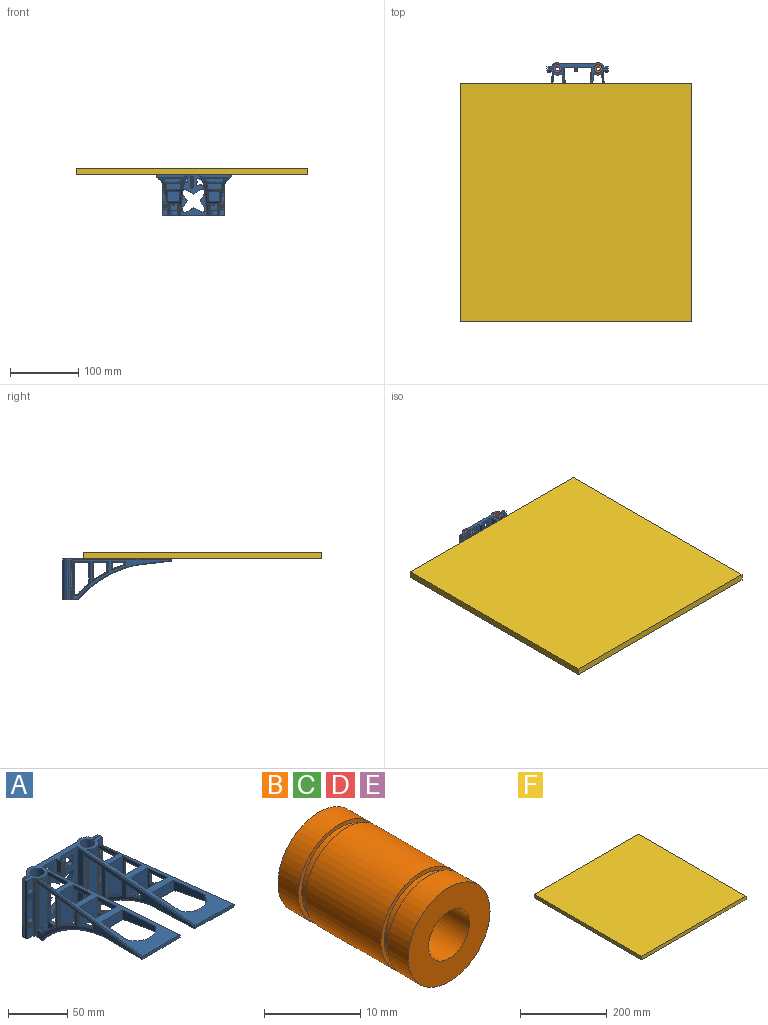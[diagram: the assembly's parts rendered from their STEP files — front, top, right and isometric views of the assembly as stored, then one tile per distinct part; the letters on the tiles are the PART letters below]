
ASSEMBLY  parts=6 mates=5
PART A: 310 faces, bbox 111.2x160.5x66.1 mm
  f0: plane 60x41.92mm, normal (0,-1,0), area 1382.5mm2, adj f11,f12,f14,f107,f146,f238,f266,f267
  f1: plane 21.16x6.51mm, normal (0,-1,0), area 128.2mm2, adj f36,f37,f131,f133
  f2: plane 10.58x6.51mm, normal (0,-1,0), area 64.1mm2, adj f11,f36,f37,f133
  f3: plane 10.58x6.51mm, normal (0,-1,0), area 64.1mm2, adj f12,f36,f37,f131
  f4: plane 23.21x4.1mm, normal (-1,-0.06,0), area 95.3mm2, adj f11,f17,f19,f86
  f5: plane 21.83x4.1mm, normal (1,-0.1,0), area 89.9mm2, adj f11,f17,f19,f89
  f6: extruded ~22.69x22.55mm, area 49.5mm2, adj f39,f43,f79,f81,f120,f121
  f7: plane 23.11x3.77mm, normal (0,0,-1), area 49.9mm2, adj f50,f52,f73,f85,f86
  f8: plane 21.34x15.62mm, normal (0,0,-1), area 35.5mm2, adj f39,f43,f70,f71,f119,f121
  f9: plane 60x2.08mm, normal (-1,0,0), area 124.6mm2, adj f11,f12,f35,f65
  f10: cylinder r=6.1mm len=60mm, axis (0,0,-1), area 2239.4mm2, adj f11,f12,f64,f65
  f11: plane 159.35x108.38mm, normal (0,0,1), area 4505.2mm2, adj f0,f2,f4,f5,f9,f10,f15,f16
  f12: plane 90.27x23.14mm, normal (0,0,-1), area 677.4mm2, adj f0,f3,f9,f10,f13,f14,f17,f18
  f13: plane 145.55x60.3mm, normal (-0.99,0.12,0), area 1183.5mm2, adj f12,f21,f37,f108,f109,f110,f111,f112
  f14: plane 153.23x60.08mm, normal (1,0.07,0), area 1761.4mm2, adj f0,f12,f21,f39,f40,f42,f44,f51
  f15: cylinder r=17.26mm len=31.2mm, axis (0,0,-1), area 201.1mm2, adj f11,f29,f38,f66
  f16: plane 21.95x20.78mm, normal (-1,-0.06,0), area 183mm2, adj f11,f30,f31,f61,f63,f68,f78,f100
  f17: cylinder r=9.14mm len=60mm, axis (0,0,-1), area 216.4mm2, adj f4,f5,f11,f12,f18,f23,f47,f51
  f18: plane 24.32x23.37mm, normal (-1,-0.06,0), area 130.6mm2, adj f12,f17,f20,f51,f83,f98,f99
  f19: plane 15.67x4.1mm, normal (0,1,0), area 64.2mm2, adj f4,f5,f11,f88
  f20: plane 16.84x5.3mm, normal (0,1,0), area 67.6mm2, adj f18,f23,f82,f83,f84,f99
  f21: plane 46.39x3.27mm, normal (0.01,-1,0), area 142.6mm2, adj f11,f13,f14,f44,f107,f108,f123
  f22: plane 22.01x21.64mm, normal (1,-0.1,0), area 196.6mm2, adj f11,f30,f31,f53,f55,f67,f77,f101
  f23: plane 23.03x22.24mm, normal (1,-0.1,0), area 124.3mm2, adj f12,f17,f20,f47,f82,f97,f99
  f24: plane 37.69x21.65mm, normal (-1,-0.06,0), area 181.2mm2, adj f11,f25,f26,f32,f42,f69,f80,f95
  f25: plane 19.91x4.1mm, normal (0,1,0), area 81.6mm2, adj f11,f24,f27,f71
  f26: plane 20.78x4.56mm, normal (0,1,0), area 74.7mm2, adj f24,f27,f79,f80,f81,f96
  f27: plane 38.84x21.78mm, normal (1,-0.1,0), area 219.9mm2, adj f11,f25,f26,f32,f43,f70,f79,f94
  f28: plane 25.94x10.71mm, normal (0,-1,0), area 266.7mm2, adj f11,f29,f38,f104,f105,f106
  f29: plane 38.47x10.01mm, normal (-1,-0.06,0), area 288.2mm2, adj f11,f15,f28,f44,f66,f104
  f30: plane 21.8x21.6mm, normal (0,-1,0), area 446.9mm2, adj f11,f16,f22,f100,f102,f103
  f31: plane 24.4x12.25mm, normal (0,1,0), area 291.8mm2, adj f11,f16,f22,f101
  f32: plane 39.11x17.46mm, normal (0,-1,0), area 636.2mm2, adj f11,f24,f27,f93,f94,f95
  f33: plane 60x49.48mm, normal (0,1,0), area 2024mm2, adj f11,f12,f34,f165,f274,f275,f276,f277
  f34: cylinder r=9.14mm len=60mm, axis (0,0,-1), area 1013.9mm2, adj f11,f12,f33,f35
  f35: plane 60x6.51mm, normal (0,1,0), area 378.1mm2, adj f9,f11,f12,f34,f125,f127
  f36: plane 60.65x3.57mm, normal (-1,0,0), area 175.4mm2, adj f1,f2,f3,f11,f12,f64,f132,f134
  f37: cylinder r=9.14mm len=60mm, axis (0,0,-1), area 195.2mm2, adj f1,f2,f3,f11,f12,f13,f108,f131
  f38: plane 35.25x10.58mm, normal (1,-0.1,0), area 276mm2, adj f11,f15,f28,f44,f66,f106
  f39: plane 27.02x15.37mm, normal (-0.07,1,0), area 378.3mm2, adj f6,f8,f14,f40,f41,f69,f71,f75
  f40: plane 21.11x4.75mm, normal (0,0,-1), area 69mm2, adj f14,f39,f42,f69
  f41: extruded ~21.04x13.08mm, area 60.6mm2, adj f39,f42,f75,f80
  f42: plane 28.85x4.03mm, normal (0.07,-1,0), area 110.2mm2, adj f14,f24,f40,f41,f69,f75,f80
  f43: plane 28.97x1.76mm, normal (0.07,-1,0), area 48.5mm2, adj f6,f8,f27,f70,f79,f121
  f44: plane 60.74x45.98mm, normal (0.01,-0.11,-0.99), area 1040.5mm2, adj f14,f21,f29,f38,f45,f66,f104,f106
  f45: extruded ~91.03x51.43mm, area 759mm2, adj f12,f44,f93,f94,f95,f96,f97,f98
  f46: plane 47.34x0.3mm, normal (0.07,-1,0), area 14.2mm2, adj f47,f49,f87,f89,f117
  f47: plane 7.77x1.97mm, normal (0,0,1), area 8.5mm2, adj f17,f23,f46,f48,f82,f87,f116,f117
  f48: extruded ~22.17x18.62mm, area 85.2mm2, adj f47,f51,f52,f76,f82,f83,f84,f114
  f49: plane 23.46x11.96mm, normal (0,0,-1), area 19.1mm2, adj f46,f52,f88,f89,f115,f117
  f50: plane 47.19x2.03mm, normal (0.07,-1,0), area 96.3mm2, adj f7,f51,f72,f85
  f51: plane 8.25x4.32mm, normal (0,0,1), area 24.4mm2, adj f14,f17,f18,f48,f50,f72,f76,f83
  f52: plane 32.76x21.8mm, normal (-0.07,1,0), area 676mm2, adj f7,f14,f48,f49,f73,f76,f86,f88
  f53: plane 12.69x2.48mm, normal (0.07,-1,0), area 27.7mm2, adj f22,f54,f56,f67,f77,f109
  f54: extruded ~18.98x7.43mm, area 40.5mm2, adj f53,f55,f77,f109,f111
  f55: plane 5.31x3.31mm, normal (-0.07,1,0), area 12.5mm2, adj f22,f54,f56,f67,f77,f110,f111,f112
  f56: plane 18.78x4.11mm, normal (0,0,-1), area 37.4mm2, adj f53,f55,f67,f109,f110
  f57: plane 7.87x1.32mm, normal (0,0,-1), area 5.3mm2, adj f59,f92
  f58: plane 11.48x2.49mm, normal (0,0,1), area 14mm2, adj f17,f59,f90,f91
  f59: plane 47.94x10.48mm, normal (0.07,-1,0), area 493.6mm2, adj f57,f58,f90,f91,f92
  f60: plane 18.6x4.84mm, normal (0,0,-1), area 65.6mm2, adj f14,f61,f63,f68
  f61: plane 5.26x4.5mm, normal (-0.07,1,0), area 17mm2, adj f14,f16,f60,f62,f68,f74,f78
  f62: extruded ~18.54x7.32mm, area 53.8mm2, adj f61,f63,f74,f78
  f63: plane 12.62x4.31mm, normal (0.07,-1,0), area 48mm2, adj f14,f16,f60,f62,f68,f74,f78
  f64: plane 60x9.04mm, normal (0,1,0), area 529.8mm2, adj f10,f11,f12,f36,f126,f128
  f65: plane 60x9.11mm, normal (0,-1,0), area 534mm2, adj f9,f10,f11,f12,f125,f127
  f66: bspline ~32.74x12.98mm, area 49.3mm2, adj f15,f29,f38,f44
  f67: plane 18.64x2.69mm, normal (0.7,-0.07,-0.71), area 22.5mm2, adj f22,f53,f55,f56
  f68: plane 18.41x2.04mm, normal (-0.71,-0.05,-0.71), area 22.2mm2, adj f16,f60,f61,f63
  f69: plane 20.91x2.2mm, normal (-0.71,-0.05,-0.71), area 25.1mm2, adj f24,f39,f40,f42,f71
  f70: plane 20.14x2.84mm, normal (0.7,-0.07,-0.71), area 23.8mm2, adj f8,f27,f43,f71
  f71: plane 21.17x0.85mm, normal (0,0.71,-0.71), area 22.1mm2, adj f8,f25,f39,f69,f70
  f72: plane 48.04x0.91mm, normal (0.76,-0.65,0), area 57.4mm2, adj f14,f50,f51,f73
  f73: plane 23.86x2.57mm, normal (0.71,0.05,-0.71), area 28.2mm2, adj f7,f14,f52,f72
  f74: bspline ~18.89x8.26mm, area 23.9mm2, adj f14,f61,f62,f63
  f75: bspline ~21.69x14.14mm, area 29.8mm2, adj f14,f39,f41,f42
  f76: bspline ~17.41x16.93mm, area 27.5mm2, adj f14,f48,f51,f52
  f77: bspline ~21.33x9.08mm, area 25mm2, adj f22,f53,f54,f55
  f78: bspline ~20.88x9mm, area 23.8mm2, adj f16,f61,f62,f63
  f79: bspline ~20.81x13.48mm, area 29mm2, adj f6,f26,f27,f43,f81
  f80: bspline ~24.14x15.58mm, area 29.4mm2, adj f24,f26,f39,f41,f42,f81
  f81: bspline ~21.58x1.61mm, area 18.3mm2, adj f6,f26,f39,f79,f80
  f82: bspline ~18.05x17.43mm, area 26.6mm2, adj f20,f23,f47,f48,f84
  f83: bspline ~17.5x16.9mm, area 26.9mm2, adj f18,f20,f48,f51,f84
  f84: bspline ~17.56x1.74mm, area 12.6mm2, adj f20,f48,f82,f83
  f85: plane 47.95x0.81mm, normal (-0.66,-0.75,0), area 51.3mm2, adj f7,f17,f50,f51,f86
  f86: plane 23.7x2.38mm, normal (-0.71,-0.05,-0.71), area 28.1mm2, adj f4,f7,f17,f52,f85,f88
  f87: plane 47.76x0.47mm, normal (0.7,-0.72,0), area 31mm2, adj f17,f46,f47,f89
  f88: plane 17.03x0.85mm, normal (0,0.71,-0.71), area 17.9mm2, adj f19,f49,f52,f86,f89
  f89: plane 22.88x3.09mm, normal (0.7,-0.07,-0.71), area 26.9mm2, adj f5,f17,f46,f49,f87,f88
  f90: plane 48.06x0.53mm, normal (0.4,-0.91,0), area 27.3mm2, adj f17,f58,f59,f92
  f91: plane 48.06x0.56mm, normal (-0.26,-0.96,0), area 27.3mm2, adj f17,f58,f59,f92
  f92: cone r=8.28mm half-angle=45deg, axis (0,0,1), area 12.2mm2, adj f17,f57,f59,f90,f91
  f93: bspline ~18.09x1.74mm, area 13.2mm2, adj f32,f45,f94,f95
  f94: bspline ~23x15.7mm, area 30.3mm2, adj f27,f32,f45,f93,f96
  f95: bspline ~23.02x15.52mm, area 31.6mm2, adj f24,f32,f45,f93,f96
  f96: bspline ~21.79x1.63mm, area 30.1mm2, adj f24,f26,f27,f45,f94,f95
  f97: bspline ~18.66x17.75mm, area 27.7mm2, adj f12,f23,f45,f99
  f98: bspline ~19.78x18.87mm, area 31.5mm2, adj f12,f18,f45,f99
  f99: bspline ~17.56x1.76mm, area 25.2mm2, adj f18,f20,f23,f45,f97,f98
  f100: bspline ~23.38x10.07mm, area 29.1mm2, adj f16,f30,f45,f101,f102
  f101: bspline ~26.26x1.42mm, area 34.5mm2, adj f16,f22,f31,f45,f100,f103
  f102: bspline ~22.49x1.61mm, area 19.7mm2, adj f30,f45,f100,f103
  f103: bspline ~23.37x10.31mm, area 28.3mm2, adj f22,f30,f45,f101,f102
  f104: bspline ~12.32x3.28mm, area 6.2mm2, adj f28,f29,f44,f45,f105
  f105: bspline ~27.13x1.36mm, area 27.6mm2, adj f28,f45,f104,f106
  f106: bspline ~15.93x4.1mm, area 8.8mm2, adj f28,f38,f44,f45,f105
  f107: plane 152.3x12.3mm, normal (0.71,0.05,0.71), area 184.1mm2, adj f0,f11,f14,f21
  f108: plane 144.42x18.78mm, normal (-0.7,0.09,0.71), area 174.9mm2, adj f11,f13,f21,f37
  f109: plane 13.03x0.96mm, normal (-0.72,-0.69,0), area 15.5mm2, adj f13,f53,f54,f56,f110,f111
  f110: plane 20.33x3.29mm, normal (-0.7,0.09,-0.71), area 23.7mm2, adj f13,f55,f56,f109,f112
  f111: bspline ~22.63x9.66mm, area 24.5mm2, adj f13,f54,f55,f109,f112
  f112: plane 4.99x0.78mm, normal (-0.69,0.72,0), area 4.7mm2, adj f13,f55,f110,f111
  f113: plane 32.07x0.78mm, normal (-0.69,0.72,0), area 34.1mm2, adj f13,f52,f114,f115
  f114: bspline ~18.2x17.49mm, area 27.1mm2, adj f13,f48,f52,f113,f116
  f115: plane 25.02x3.88mm, normal (-0.7,0.09,-0.71), area 29.4mm2, adj f13,f49,f52,f113,f117
  f116: plane 7.36x1.68mm, normal (-0.7,0.09,0.71), area 8.2mm2, adj f13,f47,f48,f114,f117
  f117: plane 48.9x0.96mm, normal (-0.72,-0.69,0), area 63.2mm2, adj f13,f46,f47,f49,f115,f116
  f118: plane 15.23x0.78mm, normal (-0.69,0.72,0), area 15.8mm2, adj f13,f39,f119,f120
  f119: plane 22.89x3.61mm, normal (-0.7,0.09,-0.71), area 26.8mm2, adj f8,f13,f39,f118,f121
  f120: bspline ~23.3x15.02mm, area 29.8mm2, adj f6,f13,f39,f118,f121
  f121: plane 29.5x0.96mm, normal (-0.72,-0.69,0), area 37mm2, adj f6,f8,f13,f43,f119,f120
  f122: bspline ~99.47x57.79mm, area 135.1mm2, adj f12,f13,f45,f123
  f123: plane 46.71x6.68mm, normal (-0.7,0.01,-0.71), area 57.6mm2, adj f13,f21,f44,f122
  f124: bspline ~97.76x57.73mm, area 120.4mm2, adj f12,f14,f44,f45
  f125: cylinder r=1.4mm len=2.8mm, axis (0,-1,0), area 18.3mm2, adj f35,f65
  f126: cylinder r=1.4mm len=4.92mm, axis (0,-1,0), area 43.3mm2, adj f64,f130
  f127: cylinder r=1.4mm len=2.8mm, axis (0,-1,0), area 18.3mm2, adj f35,f65
  f128: cylinder r=1.4mm len=4.92mm, axis (0,-1,0), area 43.3mm2, adj f64,f129
  f129: torus R=0.9mm, axis (0,-1,0), area 3.6mm2, adj f128,f131,f132
  f130: torus R=0.9mm, axis (0,-1,0), area 3.6mm2, adj f126,f133,f134
  f131: torus R=5.49mm, axis (0,1,0), area 52.8mm2, adj f1,f3,f37,f129,f132
  f132: bspline ~9.78x2.49mm, area 14.7mm2, adj f36,f129,f131
  f133: torus R=5.49mm, axis (0,1,0), area 52.8mm2, adj f1,f2,f37,f130,f134
  f134: bspline ~9.78x2.49mm, area 14.7mm2, adj f36,f130,f133
  f135: plane 21.16x6.51mm, normal (0,-1,0), area 128.2mm2, adj f167,f168,f262,f264
  f136: plane 10.58x6.51mm, normal (0,-1,0), area 64.1mm2, adj f11,f167,f168,f264
  f137: plane 10.58x6.51mm, normal (0,-1,0), area 64.1mm2, adj f12,f167,f168,f262
  f138: plane 23.21x4.1mm, normal (1,-0.06,0), area 95.3mm2, adj f11,f149,f151,f217
  f139: plane 21.83x4.1mm, normal (-1,-0.1,0), area 89.9mm2, adj f11,f149,f151,f220
  f140: extruded ~22.69x22.55mm, area 49.7mm2, adj f170,f174,f210,f212,f251,f252
  f141: plane 23.11x3.77mm, normal (0,0,-1), area 49.9mm2, adj f181,f183,f204,f216,f217
  f142: plane 21.34x15.62mm, normal (0,0,-1), area 35.5mm2, adj f170,f174,f201,f202,f250,f252
  f143: plane 60x2.08mm, normal (1,0,0), area 124.6mm2, adj f11,f12,f166,f196
  f144: cylinder r=6.1mm len=60mm, axis (0,0,-1), area 2239.4mm2, adj f11,f12,f195,f196
  f145: plane 145.55x60.3mm, normal (0.99,0.12,0), area 1183.5mm2, adj f12,f153,f168,f239,f240,f241,f242,f243
  f146: plane 153.23x60.08mm, normal (-1,0.07,0), area 1761.4mm2, adj f0,f12,f153,f170,f171,f173,f175,f182
  f147: cylinder r=17.26mm len=31.2mm, axis (0,0,-1), area 201.1mm2, adj f11,f161,f169,f197
  f148: plane 21.95x20.78mm, normal (1,-0.06,0), area 183mm2, adj f11,f162,f163,f192,f194,f199,f209,f231
  f149: cylinder r=9.14mm len=60mm, axis (0,0,-1), area 216.4mm2, adj f11,f12,f138,f139,f150,f155,f178,f182
  f150: plane 24.32x23.37mm, normal (1,-0.06,0), area 130.6mm2, adj f12,f149,f152,f182,f214,f229,f230
  f151: plane 15.67x4.1mm, normal (0,1,0), area 64.2mm2, adj f11,f138,f139,f219
  f152: plane 16.84x5.3mm, normal (0,1,0), area 67.6mm2, adj f150,f155,f213,f214,f215,f230
  f153: plane 46.39x3.27mm, normal (-0.01,-1,0), area 142.6mm2, adj f11,f145,f146,f175,f238,f239,f254
  f154: plane 22.01x21.64mm, normal (-1,-0.1,0), area 196.6mm2, adj f11,f162,f163,f184,f186,f198,f208,f232
  f155: plane 23.03x22.24mm, normal (-1,-0.1,0), area 124.3mm2, adj f12,f149,f152,f178,f213,f228,f230
  f156: plane 37.69x21.65mm, normal (1,-0.06,0), area 181.2mm2, adj f11,f157,f158,f164,f173,f200,f211,f226
  f157: plane 19.91x4.1mm, normal (0,1,0), area 81.6mm2, adj f11,f156,f159,f202
  f158: plane 20.78x4.56mm, normal (0,1,0), area 74.7mm2, adj f156,f159,f210,f211,f212,f227
  f159: plane 38.84x21.78mm, normal (-1,-0.1,0), area 219.9mm2, adj f11,f157,f158,f164,f174,f201,f210,f225
  f160: plane 25.94x10.71mm, normal (0,-1,0), area 266.7mm2, adj f11,f161,f169,f235,f236,f237
  f161: plane 38.47x10.01mm, normal (1,-0.06,0), area 288.2mm2, adj f11,f147,f160,f175,f197,f235
  f162: plane 21.8x21.6mm, normal (0,-1,0), area 446.9mm2, adj f11,f148,f154,f231,f233,f234
  f163: plane 24.4x12.25mm, normal (0,1,0), area 291.8mm2, adj f11,f148,f154,f232
  f164: plane 39.11x17.46mm, normal (0,-1,0), area 636.2mm2, adj f11,f156,f159,f224,f225,f226
  f165: cylinder r=9.14mm len=60mm, axis (0,0,-1), area 1013.9mm2, adj f11,f12,f33,f166
  f166: plane 60x6.51mm, normal (0,1,0), area 378.1mm2, adj f11,f12,f143,f165,f256,f258
  f167: plane 60.65x3.57mm, normal (1,0,0), area 175.4mm2, adj f11,f12,f135,f136,f137,f195,f263,f265
  f168: cylinder r=9.14mm len=60mm, axis (0,0,-1), area 195.2mm2, adj f11,f12,f135,f136,f137,f145,f239,f262
  f169: plane 35.25x10.58mm, normal (-1,-0.1,0), area 276mm2, adj f11,f147,f160,f175,f197,f237
  f170: plane 27.02x15.37mm, normal (0.07,1,0), area 378.3mm2, adj f140,f142,f146,f171,f172,f200,f202,f206
  f171: plane 21.11x4.75mm, normal (0,0,-1), area 69mm2, adj f146,f170,f173,f200
  f172: extruded ~21.04x13.08mm, area 60.6mm2, adj f170,f173,f206,f211
  f173: plane 28.85x4.03mm, normal (-0.07,-1,0), area 110.2mm2, adj f146,f156,f171,f172,f200,f206,f211
  f174: plane 28.97x1.76mm, normal (-0.07,-1,0), area 48.5mm2, adj f140,f142,f159,f201,f210,f252
  f175: plane 60.74x45.98mm, normal (-0.01,-0.11,-0.99), area 1040.5mm2, adj f146,f153,f161,f169,f176,f197,f235,f237
  f176: extruded ~91.03x51.43mm, area 757.6mm2, adj f12,f175,f224,f225,f226,f227,f228,f229
  f177: plane 47.34x0.3mm, normal (-0.07,-1,0), area 14.2mm2, adj f178,f180,f218,f220,f248
  f178: plane 7.77x1.97mm, normal (0,0,1), area 8.5mm2, adj f149,f155,f177,f179,f213,f218,f247,f248
  f179: extruded ~22.17x18.62mm, area 85.1mm2, adj f178,f182,f183,f207,f213,f214,f215,f245
  f180: plane 23.46x11.96mm, normal (0,0,-1), area 19.1mm2, adj f177,f183,f219,f220,f246,f248
  f181: plane 47.19x2.03mm, normal (-0.07,-1,0), area 96.3mm2, adj f141,f182,f203,f216
  f182: plane 8.25x4.32mm, normal (0,0,1), area 24.4mm2, adj f146,f149,f150,f179,f181,f203,f207,f214
  f183: plane 32.76x21.8mm, normal (0.07,1,0), area 676mm2, adj f141,f146,f179,f180,f204,f207,f217,f219
  f184: plane 12.69x2.48mm, normal (-0.07,-1,0), area 27.7mm2, adj f154,f185,f187,f198,f208,f240
  f185: extruded ~18.98x7.43mm, area 40.5mm2, adj f184,f186,f208,f240,f242
  f186: plane 5.31x3.31mm, normal (0.07,1,0), area 12.5mm2, adj f154,f185,f187,f198,f208,f241,f242,f243
  f187: plane 18.78x4.11mm, normal (0,0,-1), area 37.4mm2, adj f184,f186,f198,f240,f241
  f188: plane 7.87x1.32mm, normal (0,0,-1), area 5.3mm2, adj f190,f223
  f189: plane 11.48x2.49mm, normal (0,0,1), area 14mm2, adj f149,f190,f221,f222
  f190: plane 47.94x10.48mm, normal (-0.07,-1,0), area 493.6mm2, adj f188,f189,f221,f222,f223
  f191: plane 18.6x4.84mm, normal (0,0,-1), area 65.6mm2, adj f146,f192,f194,f199
  f192: plane 5.26x4.5mm, normal (0.07,1,0), area 17mm2, adj f146,f148,f191,f193,f199,f205,f209
  f193: extruded ~18.54x7.32mm, area 53.8mm2, adj f192,f194,f205,f209
  f194: plane 12.62x4.31mm, normal (-0.07,-1,0), area 48mm2, adj f146,f148,f191,f193,f199,f205,f209
  f195: plane 60x9.04mm, normal (0,1,0), area 529.8mm2, adj f11,f12,f144,f167,f257,f259
  f196: plane 60x9.11mm, normal (0,-1,0), area 534mm2, adj f11,f12,f143,f144,f256,f258
  f197: bspline ~34.28x15.32mm, area 49.2mm2, adj f147,f161,f169,f175
  f198: plane 18.64x2.69mm, normal (-0.7,-0.07,-0.71), area 22.5mm2, adj f154,f184,f186,f187
  f199: plane 18.41x2.04mm, normal (0.71,-0.05,-0.71), area 22.2mm2, adj f148,f191,f192,f194
  f200: plane 20.91x2.2mm, normal (0.71,-0.05,-0.71), area 25.1mm2, adj f156,f170,f171,f173,f202
  f201: plane 20.14x2.84mm, normal (-0.7,-0.07,-0.71), area 23.8mm2, adj f142,f159,f174,f202
  f202: plane 21.17x0.85mm, normal (0,0.71,-0.71), area 22.1mm2, adj f142,f157,f170,f200,f201
  f203: plane 48.04x0.91mm, normal (-0.76,-0.65,0), area 57.4mm2, adj f146,f181,f182,f204
  f204: plane 23.86x2.57mm, normal (-0.71,0.05,-0.71), area 28.2mm2, adj f141,f146,f183,f203
  f205: bspline ~18.89x8.26mm, area 23.9mm2, adj f146,f192,f193,f194
  f206: bspline ~23.81x15.48mm, area 29.8mm2, adj f146,f170,f172,f173
  f207: bspline ~19.08x18.56mm, area 27.5mm2, adj f146,f179,f182,f183
  f208: bspline ~21.33x9.08mm, area 25mm2, adj f154,f184,f185,f186
  f209: bspline ~19.02x8.25mm, area 23.8mm2, adj f148,f192,f193,f194
  f210: bspline ~20.81x13.48mm, area 29mm2, adj f140,f158,f159,f174,f212
  f211: bspline ~21.82x14.13mm, area 29.4mm2, adj f156,f158,f170,f172,f173,f212
  f212: bspline ~21.58x1.61mm, area 18.3mm2, adj f140,f158,f170,f210,f211
  f213: bspline ~18.05x17.43mm, area 26.6mm2, adj f152,f155,f178,f179,f215
  f214: bspline ~17.5x16.9mm, area 26.9mm2, adj f150,f152,f179,f182,f215
  f215: bspline ~17.56x1.74mm, area 12.6mm2, adj f152,f179,f213,f214
  f216: plane 47.95x0.81mm, normal (0.66,-0.75,0), area 51.3mm2, adj f141,f149,f181,f182,f217
  f217: plane 23.7x2.38mm, normal (0.71,-0.05,-0.71), area 28.1mm2, adj f138,f141,f149,f183,f216,f219
  f218: plane 47.76x0.47mm, normal (-0.7,-0.72,0), area 31mm2, adj f149,f177,f178,f220
  f219: plane 17.03x0.85mm, normal (0,0.71,-0.71), area 17.9mm2, adj f151,f180,f183,f217,f220
  f220: plane 22.88x3.09mm, normal (-0.7,-0.07,-0.71), area 26.9mm2, adj f139,f149,f177,f180,f218,f219
  f221: plane 48.06x0.53mm, normal (-0.4,-0.91,0), area 27.3mm2, adj f149,f189,f190,f223
  f222: plane 48.06x0.56mm, normal (0.26,-0.96,0), area 27.3mm2, adj f149,f189,f190,f223
  f223: cone r=8.28mm half-angle=45deg, axis (0,0,1), area 12.2mm2, adj f149,f188,f190,f221,f222
  f224: bspline ~18.09x1.74mm, area 13.2mm2, adj f164,f176,f225,f226
  f225: bspline ~23x15.7mm, area 30.3mm2, adj f159,f164,f176,f224,f227
  f226: bspline ~23.02x15.52mm, area 31.6mm2, adj f156,f164,f176,f224,f227
  f227: bspline ~21.79x1.63mm, area 30.1mm2, adj f156,f158,f159,f176,f225,f226
  f228: bspline ~18.66x17.75mm, area 27.7mm2, adj f12,f155,f176,f230
  f229: bspline ~19.78x18.87mm, area 31.5mm2, adj f12,f150,f176,f230
  f230: bspline ~17.56x1.76mm, area 25.2mm2, adj f150,f152,f155,f176,f228,f229
  f231: bspline ~23.38x10.07mm, area 29.1mm2, adj f148,f162,f176,f232,f233
  f232: bspline ~26.26x1.42mm, area 34.5mm2, adj f148,f154,f163,f176,f231,f234
  f233: bspline ~22.49x1.61mm, area 19.7mm2, adj f162,f176,f231,f234
  f234: bspline ~23.37x10.31mm, area 28.3mm2, adj f154,f162,f176,f232,f233
  f235: bspline ~12.32x3.28mm, area 6.2mm2, adj f160,f161,f175,f176,f236
  f236: bspline ~27.13x1.36mm, area 27.6mm2, adj f160,f176,f235,f237
  f237: bspline ~15.93x4.1mm, area 8.8mm2, adj f160,f169,f175,f176,f236
  f238: plane 152.3x12.3mm, normal (-0.71,0.05,0.71), area 184.1mm2, adj f0,f11,f146,f153
  f239: plane 144.42x18.78mm, normal (0.7,0.09,0.71), area 174.9mm2, adj f11,f145,f153,f168
  f240: plane 13.03x0.96mm, normal (0.72,-0.69,0), area 15.5mm2, adj f145,f184,f185,f187,f241,f242
  f241: plane 20.33x3.29mm, normal (0.7,0.09,-0.71), area 23.7mm2, adj f145,f186,f187,f240,f243
  f242: bspline ~22.63x9.66mm, area 24.5mm2, adj f145,f185,f186,f240,f243
  f243: plane 4.99x0.78mm, normal (0.69,0.72,0), area 4.7mm2, adj f145,f186,f241,f242
  f244: plane 32.07x0.78mm, normal (0.69,0.72,0), area 34.1mm2, adj f145,f183,f245,f246
  f245: bspline ~19.95x19.18mm, area 27.1mm2, adj f145,f179,f183,f244,f247
  f246: plane 25.02x3.88mm, normal (0.7,0.09,-0.71), area 29.4mm2, adj f145,f180,f183,f244,f248
  f247: plane 7.36x1.68mm, normal (0.7,0.09,0.71), area 8.2mm2, adj f145,f178,f179,f245,f248
  f248: plane 48.9x0.96mm, normal (0.72,-0.69,0), area 63.2mm2, adj f145,f177,f178,f180,f246,f247
  f249: plane 15.23x0.78mm, normal (0.69,0.72,0), area 15.8mm2, adj f145,f170,f250,f251
  f250: plane 22.89x3.61mm, normal (0.7,0.09,-0.71), area 26.8mm2, adj f142,f145,f170,f249,f252
  f251: bspline ~25.58x16.45mm, area 29.9mm2, adj f140,f145,f170,f249,f252
  f252: plane 29.5x0.96mm, normal (0.72,-0.69,0), area 37mm2, adj f140,f142,f145,f174,f250,f251
  f253: bspline ~90.91x52.78mm, area 135.1mm2, adj f12,f145,f176,f254
  f254: plane 46.71x6.68mm, normal (0.7,0.01,-0.71), area 57.6mm2, adj f145,f153,f175,f253
  f255: bspline ~97.76x57.73mm, area 120.4mm2, adj f12,f146,f175,f176
  f256: cylinder r=1.4mm len=2.8mm, axis (0,-1,0), area 18.3mm2, adj f166,f196
  f257: cylinder r=1.4mm len=4.92mm, axis (0,-1,0), area 43.3mm2, adj f195,f261
  f258: cylinder r=1.4mm len=2.8mm, axis (0,-1,0), area 18.3mm2, adj f166,f196
  f259: cylinder r=1.4mm len=4.92mm, axis (0,-1,0), area 43.3mm2, adj f195,f260
  f260: torus R=0.9mm, axis (0,-1,0), area 3.6mm2, adj f259,f262,f263
  f261: torus R=0.9mm, axis (0,-1,0), area 3.6mm2, adj f257,f264,f265
  f262: torus R=5.49mm, axis (0,1,0), area 52.8mm2, adj f135,f137,f168,f260,f263
  f263: bspline ~9.78x2.49mm, area 14.7mm2, adj f167,f260,f262
  f264: torus R=5.49mm, axis (0,1,0), area 52.8mm2, adj f135,f136,f168,f261,f265
  f265: bspline ~9.78x2.49mm, area 14.7mm2, adj f167,f261,f264
  f266: plane 6x5mm, normal (-1,0,0), area 25.1mm2, adj f0,f286,f295,f297,f299
  f267: plane 6x0.17mm, normal (0,0,-1), area 1mm2, adj f0,f294,f304,f307
  f268: plane 6x5mm, normal (1,0,0), area 25.1mm2, adj f0,f286,f288,f291,f292
  f269: plane 13x6mm, normal (1,0,0), area 78mm2, adj f0,f11,f287,f288
  f270: plane 13x6mm, normal (-1,0,0), area 78mm2, adj f0,f11,f299,f301
  f271: plane 19x2.17mm, normal (0,-1,0), area 29.3mm2, adj f11,f290,f294,f298,f302,f305,f308,f309
  f272: cylinder r=1.4mm len=15mm, axis (0,0,1), area 131.9mm2, adj f11,f273
  f273: plane 2.8x2.8mm, normal (0,0,1), area 6.2mm2, adj f272
  f274: extruded ~6.02x5.39mm, area 58.2mm2, adj f0,f33,f275,f277
  f275: extruded ~6.02x5.39mm, area 58.2mm2, adj f0,f33,f274,f276
  f276: extruded ~6.02x5.39mm, area 58.2mm2, adj f0,f33,f275,f277
  f277: extruded ~6.02x5.39mm, area 58.2mm2, adj f0,f33,f274,f276
  f278: extruded ~5x3.7mm, area 40.4mm2, adj f0,f33,f279,f281
  f279: extruded ~5x3.71mm, area 40.4mm2, adj f0,f33,f278,f280
  f280: extruded ~5x3.7mm, area 40.4mm2, adj f0,f33,f279,f281
  f281: extruded ~5x3.71mm, area 40.4mm2, adj f0,f33,f278,f280
  f282: extruded ~16.68x16.64mm, area 181mm2, adj f0,f33,f283,f285
  f283: extruded ~16.76x16.55mm, area 181mm2, adj f0,f33,f282,f284
  f284: extruded ~16.68x16.64mm, area 181mm2, adj f0,f33,f283,f285
  f285: extruded ~16.76x16.55mm, area 181mm2, adj f0,f33,f282,f284
  f286: cylinder r=1.25mm len=3mm, axis (1,0,0), area 23.6mm2, adj f266,f268
  f287: plane 13x0.71mm, normal (0.71,-0.71,0), area 13mm2, adj f11,f269,f289,f309
  f288: plane 6x1mm, normal (0.71,0,-0.71), area 8.5mm2, adj f0,f268,f269,f289
  f289: plane 1.04x1.04mm, normal (0.58,-0.58,-0.58), area 0.8mm2, adj f287,f288,f290,f309
  f290: plane 1.46x1.04mm, normal (0,-0.71,-0.71), area 0.7mm2, adj f271,f289,f291,f302,f309
  f291: plane 5.71x0.71mm, normal (0.71,-0.71,0), area 5.4mm2, adj f268,f290,f293,f302
  f292: plane 6x0.71mm, normal (0.71,0,-0.71), area 6mm2, adj f0,f268,f293,f304
  f293: plane 0.74x0.74mm, normal (0.58,-0.58,-0.58), area 0.5mm2, adj f291,f292,f302,f303,f304
  f294: plane 1x1mm, normal (0,-0.71,-0.71), area 0.5mm2, adj f267,f271,f302,f303,f304,f305,f306,f307
  f295: plane 6x0.71mm, normal (-0.71,0,-0.71), area 6mm2, adj f0,f266,f296,f307
  f296: plane 0.74x0.74mm, normal (-0.58,-0.58,-0.58), area 0.5mm2, adj f295,f297,f305,f306,f307
  f297: plane 5.71x0.71mm, normal (-0.71,-0.71,0), area 5.4mm2, adj f266,f296,f298,f305
  f298: plane 1.46x1.04mm, normal (0,-0.71,-0.71), area 0.7mm2, adj f271,f297,f300,f305,f308
  f299: plane 6x1mm, normal (-0.71,0,-0.71), area 8.5mm2, adj f0,f266,f270,f300
  f300: plane 1.04x1.04mm, normal (-0.58,-0.58,-0.58), area 0.8mm2, adj f298,f299,f301,f308
  f301: plane 13x0.71mm, normal (-0.71,-0.71,0), area 13mm2, adj f11,f270,f300,f308
  f302: cylinder r=1mm len=6mm, axis (0,0,1), area 4.6mm2, adj f271,f290,f291,f293,f294,f303
  f303: cylinder r=1mm len=1.12mm, axis (0,-0.71,0.71), area 0.8mm2, adj f293,f294,f302,f304
  f304: cylinder r=1mm len=6mm, axis (0,-1,0), area 4.7mm2, adj f0,f267,f292,f293,f294,f303
  f305: cylinder r=1mm len=6mm, axis (0,0,1), area 4.6mm2, adj f271,f294,f296,f297,f298,f306
  f306: cylinder r=1mm len=1.12mm, axis (0,-0.71,0.71), area 0.8mm2, adj f294,f296,f305,f307
  f307: cylinder r=1mm len=6mm, axis (0,-1,0), area 4.7mm2, adj f0,f267,f294,f295,f296,f306
  f308: cylinder r=1mm len=13.09mm, axis (0,0,1), area 10.2mm2, adj f11,f271,f298,f300,f301
  f309: cylinder r=1mm len=13.09mm, axis (0,0,1), area 10.2mm2, adj f11,f271,f287,f289,f290
PART B: 12 faces, bbox 12x19.1x12 mm
  f0: cylinder r=3mm len=19.1mm, axis (0,1,0), area 360mm2, adj f3,f10
  f1: cylinder r=6mm len=12mm, axis (0,1,0), area 113.1mm2, adj f2,f3
  f2: plane 12x12mm, normal (0,-1,0), area 18.1mm2, adj f1,f4
  f3: plane 12x12mm, normal (0,1,0), area 84.8mm2, adj f0,f1
  f4: cylinder r=5.5mm len=11mm, axis (0,1,0), area 34.6mm2, adj f2,f7
  f5: cylinder r=6mm len=12mm, axis (0,1,0), area 418.5mm2, adj f6,f7
  f6: plane 12x12mm, normal (0,-1,0), area 18.1mm2, adj f5,f8
  f7: plane 12x12mm, normal (0,1,0), area 18.1mm2, adj f4,f5
  f8: cylinder r=5.5mm len=11mm, axis (0,1,0), area 34.6mm2, adj f6,f11
  f9: cylinder r=6mm len=12mm, axis (0,1,0), area 113.1mm2, adj f10,f11
  f10: plane 12x12mm, normal (0,-1,0), area 84.8mm2, adj f0,f9
  f11: plane 12x12mm, normal (0,1,0), area 18.1mm2, adj f8,f9
PART C: same geometry as B
PART D: same geometry as B
PART E: same geometry as B
PART F: 6 faces, bbox 340x350x10 mm
  f0: plane 340x10mm, normal (0,1,0), area 3400mm2, adj f1,f3,f4,f5
  f1: plane 350x10mm, normal (-1,0,0), area 3500mm2, adj f0,f2,f4,f5
  f2: plane 340x10mm, normal (0,-1,0), area 3400mm2, adj f1,f3,f4,f5
  f3: plane 350x10mm, normal (1,0,0), area 3500mm2, adj f0,f2,f4,f5
  f4: plane 350x340mm, normal (0,0,1), area 119000mm2, adj f0,f1,f2,f3
  f5: plane 350x340mm, normal (0,0,-1), area 119000mm2, adj f0,f1,f2,f3
PLACE A t=(-6.1,-0.08,0)mm
PLACE B rot(axis=(-1,0,0),90deg) t=(25.62,-2.55,40.9)mm
PLACE C rot(axis=(-1,0,0),90deg) t=(25.62,-2.55,0)mm
PLACE D rot(axis=(-1,0,0),90deg) t=(-34.38,-2.55,0)mm
PLACE E rot(axis=(-1,0,0),90deg) t=(-34.38,-2.55,40.9)mm
PLACE F rot(axis=(-1,0,0),0deg) t=(-132.01,-231.77,60)mm
MATE fastened B.f0 <-> A.f144  axis (0,0,1) through (25.62,-2.55,60)mm
MATE fastened A.f10 <-> D.f0  axis (0,0,-1) through (-34.38,-2.55,0)mm
MATE fastened F.f5 <-> A.f11  axis (0,0,-1) through (-6.88,-23.58,60)mm
MATE fastened C.f0 <-> A.f144  axis (0,0,-1) through (25.62,-2.55,0)mm
MATE fastened E.f0 <-> A.f10  axis (0,0,1) through (-34.38,-2.55,60)mm
